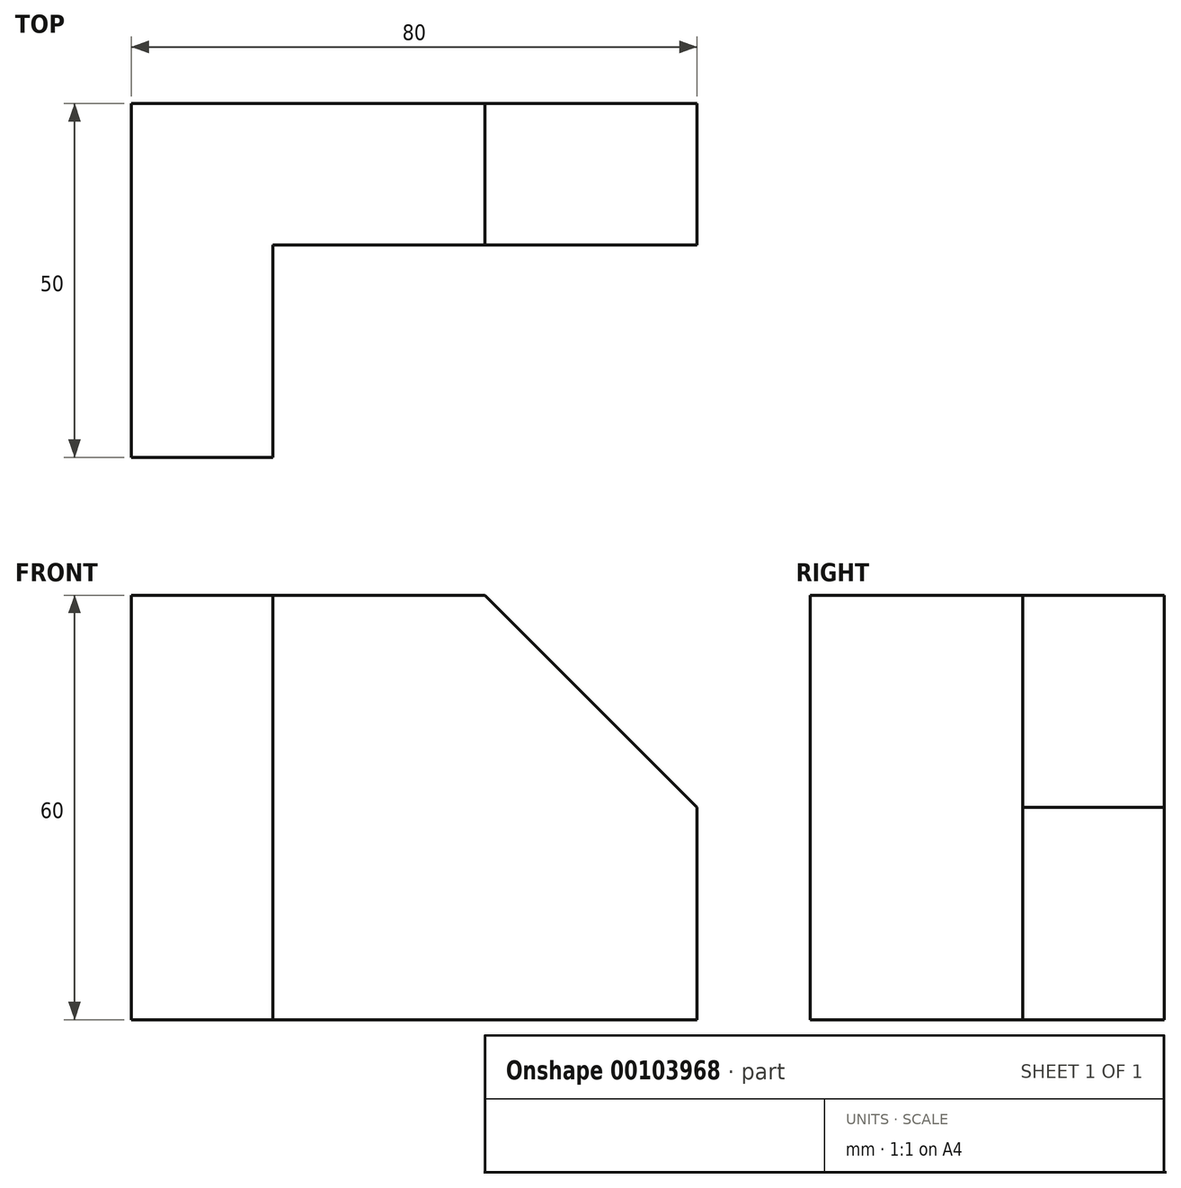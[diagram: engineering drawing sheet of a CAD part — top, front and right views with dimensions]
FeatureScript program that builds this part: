
annotation { "Feature Type Name" : "Feature", "Feature Type Description" : "" }
export const myFeature = defineFeature(function(context is Context, id is Id, definition is map)
    precondition{}
    {
        {
            var Q0;
            Q0=qCreatedBy(makeId("Front.planeOp"),FACE);
            var sketch = newSketch(context, id + "F0", { "sketchPlane" : qUnion([Q0])});
            skLineSegment(sketch, "E0.bottom", {"start": v(10, 30) * mm, "end": v(-40, 30) * mm});
            skLineSegment(sketch, "E0.top", {"start": v(40, -30) * mm, "end": v(-40, -30) * mm});
            skLineSegment(sketch, "E0.left", {"start": v(40, 0) * mm, "end": v(40, -30) * mm});
            skLineSegment(sketch, "E0.right", {"start": v(-40, 30) * mm, "end": v(-40, -30) * mm});
            skPoint(sketch, "E0.middle", {"position": v(0, 0) * mm});
            skLineSegment(sketch, "E1", {"start": v(-20, 30) * mm, "end": v(-20, -30) * mm});
            skLineSegment(sketch, "E2", {"start": v(10, 30) * mm, "end": v(40, 0) * mm});
            skPoint(sketch, "E3.orphan", {"position": v(40, 30) * mm});
            skSolve(sketch);
        }
        {
            var Q0;
            {var subQ0=sQuery(id+"F0.wireOp",EDGE,"E0.right");Q0=makeQuery(id+"F0.imprint","IMPRINT",FACE,{"disambiguationData":[TD([[makeQuery(id+"F0.imprint","IMPRINT",EDGE,{"derivedFrom":subQ0}),1.0]])]});}
            var Q1;
            {var subQ1=sQuery(id+"F0.wireOp",EDGE,"E0.left");Q1=makeQuery(id+"F0.imprint","IMPRINT",FACE,{"disambiguationData":[TD([[makeQuery(id+"F0.imprint","IMPRINT",EDGE,{"derivedFrom":subQ1}),-1.0]])]});}
            extrude(context, id + "F1", {"entities" : qUnion([Q0, Q1]), "depth" : 20 * mm, "offsetDistance" : 25 * mm});
        }
        {
            var Q0;
            Q0=makeQuery(id+"F1.opExtrude","CAP_FACE",FACE,{"disambiguationData":[OSD([sQuery(id+"F0.wireOp",EDGE,"E0.bottom"),sQuery(id+"F0.wireOp",EDGE,"E0.top"),sQuery(id+"F0.wireOp",EDGE,"E0.left"),sQuery(id+"F0.wireOp",EDGE,"E0.right"),sQuery(id+"F0.wireOp",EDGE,"E2")])],"isStart":false});
            var sketch = newSketch(context, id + "F2", { "sketchPlane" : qUnion([Q0])});
            skLineSegment(sketch, "E4", {"start": v(-20, 30) * mm, "end": v(-20, -30) * mm});
            skSolve(sketch);
        }
        {
            var Q0;
            Q0 = qSketchRegion(id + "F2", true);
            var Q1;
            {var subQ0=sQuery(id+"F2.wireOp",EDGE,"E4");Q1=makeQuery(id+"F2.imprint","IMPRINT",FACE,{"disambiguationData":[TD([[makeQuery(id+"F2.imprint","IMPRINT",EDGE,{"derivedFrom":subQ0}),-1.0]])]});}
            extrude(context, id + "F3", {"entities" : qUnion([Q0, Q1]), "operationType" : NewBodyOperationType.ADD, "depth" : 30 * mm, "offsetDistance" : 25 * mm});
        }
    });
